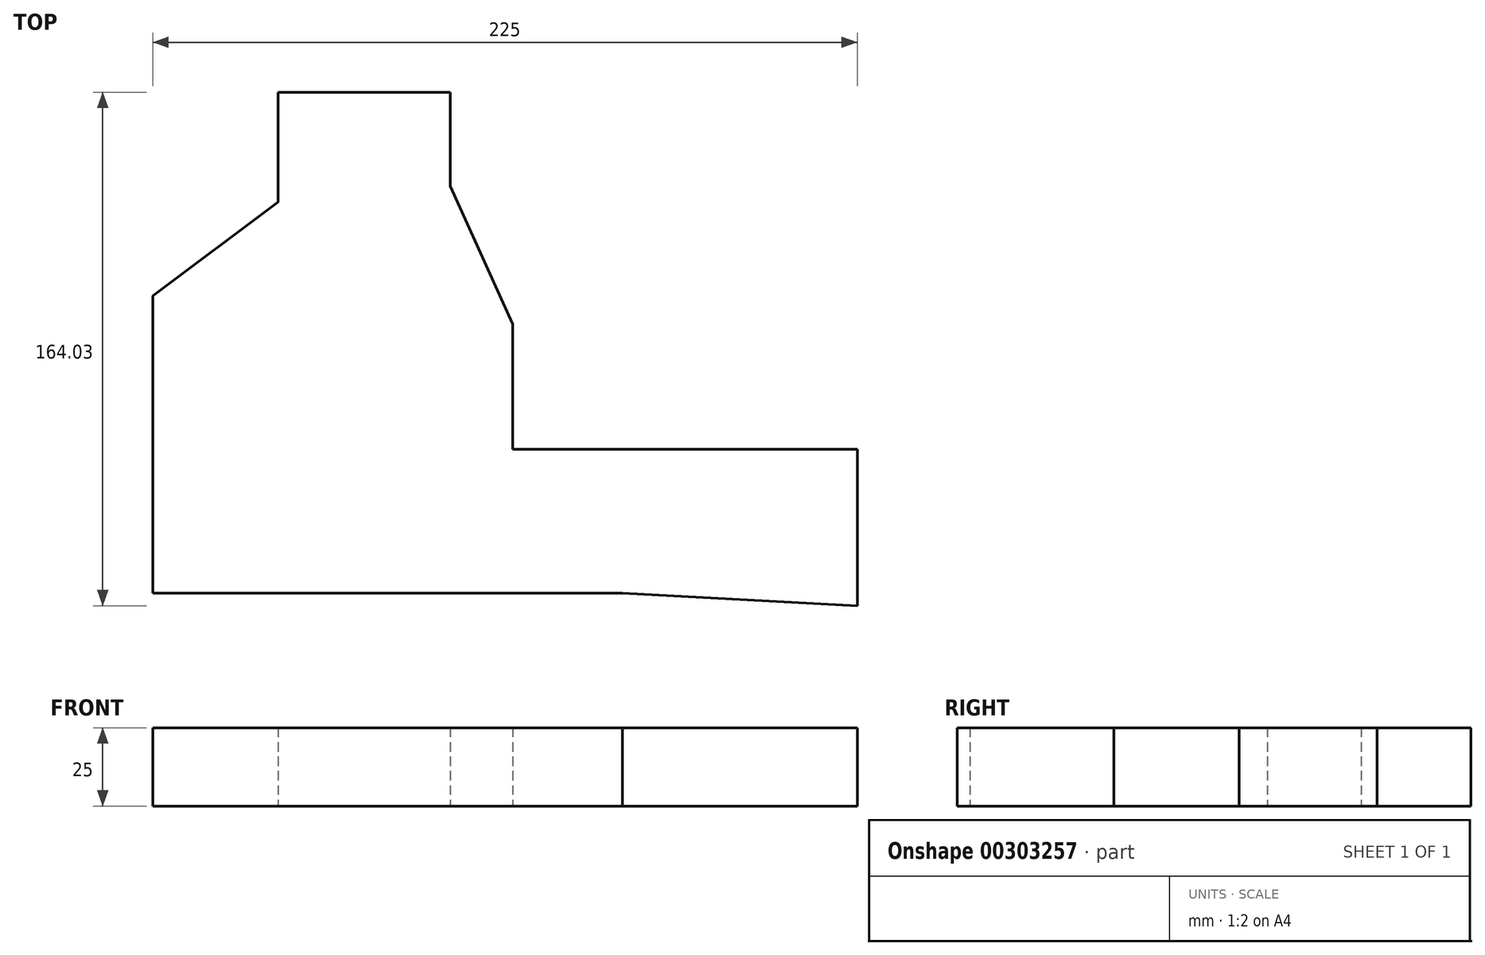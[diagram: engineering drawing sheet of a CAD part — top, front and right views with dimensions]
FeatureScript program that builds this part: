
annotation { "Feature Type Name" : "Feature", "Feature Type Description" : "" }
export const myFeature = defineFeature(function(context is Context, id is Id, definition is map)
    precondition{}
    {
        {
            var Q0;
            Q0=qCreatedBy(makeId("Top.planeOp"),FACE);
            var sketch = newSketch(context, id + "F0", { "sketchPlane" : qUnion([Q0])});
            skLineSegment(sketch, "E0", {"start": v(-36.46, 56.2) * mm, "end": v(18.54, 56.2) * mm});
            skLineSegment(sketch, "E1", {"start": v(-36.46, 56.2) * mm, "end": v(-36.46, 21.2) * mm});
            skLineSegment(sketch, "E2", {"start": v(-36.46, 21.2) * mm, "end": v(-76.46, -8.8) * mm});
            skLineSegment(sketch, "E3", {"start": v(-76.46, -8.8) * mm, "end": v(-76.46, -103.8) * mm});
            skLineSegment(sketch, "E4", {"start": v(-76.46, -103.8) * mm, "end": v(73.54, -103.8) * mm});
            skLineSegment(sketch, "E5", {"start": v(38.54, -57.82) * mm, "end": v(38.54, -17.82) * mm});
            skLineSegment(sketch, "E6", {"start": v(38.54, -17.82) * mm, "end": v(18.54, 26.2) * mm});
            skLineSegment(sketch, "E7", {"start": v(18.54, 26.2) * mm, "end": v(18.54, 56.2) * mm});
            skPoint(sketch, "E8.end.orphan", {"position": v(18.54, -30.6) * mm});
            skPoint(sketch, "E9.end.orphan", {"position": v(-36.46, 3.98) * mm});
            skPoint(sketch, "E10.start.orphan", {"position": v(-76.46, 21.2) * mm});
            skLineSegment(sketch, "E11", {"start": v(73.54, -103.8) * mm, "end": v(148.54, -107.82) * mm});
            skLineSegment(sketch, "E12", {"start": v(148.54, -107.82) * mm, "end": v(148.54, -57.82) * mm});
            skPoint(sketch, "E13.start.orphan", {"position": v(143.54, -57.82) * mm});
            skLineSegment(sketch, "E14", {"start": v(38.54, -57.82) * mm, "end": v(148.54, -57.82) * mm});
            skSolve(sketch);
        }
        {
            var Q0;
            Q0=makeQuery(id+"F0.imprint","IMPRINT",FACE,{"disambiguationData":[TD([[makeQuery(id+"F0.imprint","IMPRINT",EDGE,{"derivedFrom":sQuery(id+"F0.wireOp",EDGE,"E0")}),-1.0]])]});
            extrude(context, id + "F1", {"entities" : qUnion([Q0]), "depth" : 25 * mm});
        }
    });
